FCSTD DOCUMENT  (FreeCAD 0.20R29603 (Git))
Label: Heat Exchanger inlet dispersion grid rounded edges
License: All rights reserved
LicenseURL: http://en.wikipedia.org/wiki/All_rights_reserved
objects: Sketcher::SketchObject×3, Spreadsheet::Sheet×1, PartDesign::Body×1
note: 4 computed .brp shape members not serialized (recipe doc carries the construction recipe); baked Part::Feature solids carry a one-line shape summary decoded from their .brp

FEATURE [Sketcher::SketchObject] Sketch
  Base_da = 2
  FullyConstrained = true
  MapMode = 5
  Support = -> [XY_Plane]
  expr: Constraints[100] = 5 * Base_da
  expr: Constraints[101] = 4 * Base_da
  expr: Constraints[102] = 3 * Base_da
  expr: Constraints[103] = 2 * Base_da
  expr: Constraints[105] = Base_da
  sketch-geometry (47):
    g0: LineSegment StartX=10 StartY=0 StartZ=0 EndX=10 EndY=10 EndZ=0
    g1: LineSegment StartX=20 StartY=0 StartZ=0 EndX=20.349 EndY=9.99391 EndZ=0
    g2: LineSegment StartX=10 StartY=0 StartZ=0 EndX=20 EndY=0 EndZ=0
    g3: LineSegment StartX=30 StartY=0 StartZ=0 EndX=31.0453 EndY=9.94522 EndZ=0
    g4: LineSegment StartX=20 StartY=0 StartZ=0 EndX=30 EndY=0 EndZ=0
    g5: LineSegment StartX=40 StartY=0 StartZ=0 EndX=42.0791 EndY=9.78148 EndZ=0
    g6: LineSegment StartX=30 StartY=0 StartZ=0 EndX=40 EndY=0 EndZ=0
    g7: LineSegment StartX=50 StartY=0 StartZ=0 EndX=53.4202 EndY=9.39693 EndZ=0
    g8: LineSegment StartX=40 StartY=0 StartZ=0 EndX=50 EndY=0 EndZ=0
    g9: LineSegment StartX=60 StartY=0 StartZ=0 EndX=65 EndY=8.66025 EndZ=0
    g10: LineSegment StartX=50 StartY=0 StartZ=0 EndX=60 EndY=0 EndZ=0
    g11: ArcOfCircle CenterX=0 CenterY=0 CenterZ=0 NormalX=0 NormalY=0 NormalZ=1 AngleXU=0 Radius=80 StartAngle=0 EndAngle=1.5708
    g12: ArcOfParabola CenterX=68.3381 CenterY=12.9026 CenterZ=0 NormalX=0 NormalY=0 NormalZ=1 Focal=8.86174 AngleXU=-0.816138 StartAngle=-5.33797 EndAngle=10.3906
    g13: GeomPoint X=74.4087 Y=6.44675 Z=0
    g14: LineSegment StartX=68.3381 StartY=12.9026 StartZ=0 EndX=74.4087 EndY=6.44675 EndZ=0
    g15: ArcOfParabola CenterX=75.2671 CenterY=35.9454 CenterZ=0 NormalX=0 NormalY=0 NormalZ=1 Focal=10.5647 AngleXU=-1.28196 StartAngle=-28.5038 EndAngle=-3.40911
    g16: GeomPoint X=78.2762 Y=25.8183 Z=0
    g17: LineSegment StartX=75.2671 StartY=35.9454 StartZ=0 EndX=78.2762 EndY=25.8183 EndZ=0
    g18: ArcOfParabola CenterX=69.0582 CenterY=53.9908 CenterZ=0 NormalX=0 NormalY=0 NormalZ=1 Focal=16.8881 AngleXU=-1.12039 StartAngle=-43.5341 EndAngle=-7.65215
    g19: GeomPoint X=76.4101 Y=38.7869 Z=0
    g20: LineSegment StartX=69.0582 StartY=53.9908 StartZ=0 EndX=76.4101 EndY=38.7869 EndZ=0
    g21: ArcOfParabola CenterX=58.9375 CenterY=71.8255 CenterZ=0 NormalX=0 NormalY=0 NormalZ=1 Focal=31.4249 AngleXU=-0.875633 StartAngle=-61.0548 EndAngle=-12.8996
    g22: GeomPoint X=79.0655 Y=47.6928 Z=0
    g23: LineSegment StartX=58.9375 StartY=71.8255 StartZ=0 EndX=79.0655 EndY=47.6928 EndZ=0
    g24: ArcOfParabola CenterX=41.678 CenterY=84.7017 CenterZ=0 NormalX=0 NormalY=0 NormalZ=1 Focal=64.3816 AngleXU=-0.560144 StartAngle=-74.6231 EndAngle=-14.3967
    g25: GeomPoint X=96.2207 Y=50.4952 Z=0
    g26: LineSegment StartX=41.678 StartY=84.7017 StartZ=0 EndX=96.2207 EndY=50.4952 EndZ=0
    g27: ArcOfParabola CenterX=10.3255 CenterY=-3.7979 CenterZ=0 NormalX=0 NormalY=0 NormalZ=1 Focal=146.058 AngleXU=0.0471993 StartAngle=13.7979 EndAngle=81.3483
    g28: GeomPoint X=156.22 Y=3.09336 Z=0
    g29: LineSegment StartX=10.3255 StartY=-3.7979 StartZ=0 EndX=156.22 EndY=3.09336 EndZ=0
    g30: LineSegment StartX=17.8017 StartY=77.9942 StartZ=0 EndX=3.6e-15 EndY=80 EndZ=0
    g31: LineSegment StartX=17.8017 StartY=77.9942 StartZ=0 EndX=34.7107 EndY=72.0775 EndZ=0
    g32: LineSegment StartX=34.7107 StartY=72.0775 StartZ=0 EndX=49.8792 EndY=62.5465 EndZ=0
    g33: LineSegment StartX=49.8792 StartY=62.5465 StartZ=0 EndX=62.5465 EndY=49.8792 EndZ=0
    g34: LineSegment StartX=62.5465 StartY=49.8792 StartZ=0 EndX=72.0775 EndY=34.7107 EndZ=0
    g35: LineSegment StartX=77.9942 StartY=17.8017 StartZ=0 EndX=72.0775 EndY=34.7107 EndZ=0
    g36: LineSegment StartX=77.9942 StartY=17.8017 StartZ=0 EndX=80 EndY=0 EndZ=0
    g37: LineSegment StartX=17.8017 StartY=77.9942 StartZ=0 EndX=20.0269 EndY=87.7435 EndZ=0
    g38: LineSegment StartX=77.9942 StartY=17.8017 StartZ=0 EndX=87.7435 EndY=20.0269 EndZ=0
    g39: LineSegment StartX=72.0775 StartY=34.7107 StartZ=0 EndX=81.0872 EndY=39.0495 EndZ=0
    g40: LineSegment StartX=62.5465 StartY=49.8792 StartZ=0 EndX=70.3648 EndY=56.1141 EndZ=0
    g41: LineSegment StartX=49.8792 StartY=62.5465 StartZ=0 EndX=56.1141 EndY=70.3648 EndZ=0
    g42: LineSegment StartX=34.7107 StartY=72.0775 StartZ=0 EndX=39.0495 EndY=81.0872 EndZ=0
    g43: LineSegment StartX=60 StartY=0 StartZ=0 EndX=70 EndY=0 EndZ=0
    g44: ArcOfCircle CenterX=75.2269 CenterY=0.670424 CenterZ=0 NormalX=0 NormalY=0 NormalZ=1 AngleXU=0 Radius=3.39097 StartAngle=0.467529 EndAngle=1.4226
    g45: ArcOfCircle CenterX=84.4513 CenterY=5.32744 CenterZ=0 NormalX=0 NormalY=0 NormalZ=1 AngleXU=0 Radius=6.94229 StartAngle=3.60912 EndAngle=4.01635
    g46: LineSegment StartX=70 StartY=0 StartZ=0 EndX=75.7276 EndY=4.02423 EndZ=0
  constraints (117):
    c: PointOnObject(g0,g-1)
    c: DistanceX(g-1,g0) = 10
    c: Coincident(g0,g2)
    c: Coincident(g1,g2)
    c: Distance(g2) = 10
    c: Coincident(g1,g4)
    c: Coincident(g3,g4)
    c: Equal(g2,g4)
    c: Parallel(g4,g2)
    c: Coincident(g3,g6)
    c: Coincident(g5,g6)
    c: Equal(g2,g6)
    c: Parallel(g6,g2)
    c: Coincident(g5,g8)
    c: Coincident(g7,g8)
    c: Equal(g2,g8)
    c: Parallel(g8,g2)
    c: Coincident(g7,g10)
    c: Coincident(g9,g10)
    c: Equal(g2,g10)
    c: Parallel(g10,g2)
    c: PointOnObject(g1,g-1)
    c: InternalAlignment(g13,g12)
    c: Coincident(g13,g14)
    c: Coincident(g12,g14)
    c: InternalAlignment(g16,g15)
    c: Coincident(g16,g17)
    c: Coincident(g15,g17)
    c: Tangent(g12,g9) = -1.5708
    c: Tangent(g15,g7) = -1.5708
    c: Equal(g9,g7)
    c: Equal(g7,g5)
    c: Equal(g5,g3)
    c: Equal(g3,g1)
    c: Equal(g1,g0)
    c: DistanceY(g0,g0) = 10
    c: PointOnObject(g15,g11)
    c: DistanceX(g11,g11) = 80
    c: Coincident(g-1,g11)
    c: PointOnObject(g11,g-1)
    c: PointOnObject(g12,g11)
    c: InternalAlignment(g19,g18)
    c: Coincident(g19,g20)
    c: Coincident(g18,g20)
    c: PointOnObject(g18,g11)
    c: InternalAlignment(g22,g21)
    c: Coincident(g22,g23)
    c: Coincident(g21,g23)
    c: PointOnObject(g21,g11)
    c: InternalAlignment(g25,g24)
    c: Coincident(g25,g26)
    c: Coincident(g24,g26)
    c: PointOnObject(g24,g11)
    c: InternalAlignment(g28,g27)
    c: Coincident(g28,g29)
    c: Coincident(g27,g29)
    c: PointOnObject(g27,g11)
    c: Tangent(g18,g5) = -1.5708
    c: Tangent(g21,g3) = -1.5708
    c: Tangent(g24,g1) = -1.5708
    c: Tangent(g27,g0) = -1.5708
    c: PointOnObject(g11,g-2)
    c: Coincident(g30,g27)
    c: Coincident(g30,g11)
    c: Coincident(g31,g27)
    c: Coincident(g31,g24)
    c: Coincident(g32,g24)
    c: Coincident(g32,g21)
    c: Coincident(g33,g21)
    c: Coincident(g33,g18)
    c: Coincident(g34,g18)
    c: Coincident(g34,g15)
    c: Coincident(g35,g12)
    c: Coincident(g35,g15)
    c: Coincident(g36,g12)
    c: Coincident(g36,g11)
    c: Equal(g36,g35)
    c: Equal(g35,g34)
    c: Equal(g33,g34)
    c: Equal(g32,g33)
    c: Equal(g31,g32)
    c: Equal(g30,g31)
    c: Perpendicular(g11,g38)
    c: Tangent(g38,g12) = -1.5708
    c: Perpendicular(g11,g39)
    c: Tangent(g39,g15) = -1.5708
    c: Perpendicular(g11,g40)
    c: Tangent(g40,g18) = -1.5708
    c: Perpendicular(g11,g41)
    c: Perpendicular(g11,g42)
    c: Tangent(g42,g24) = -1.5708
    c: Tangent(g41,g21) = -1.5708
    c: Equal(g38,g39)
    c: Equal(g39,g40)
    c: Equal(g40,g41)
    c: Equal(g41,g42)
    c: Equal(g42,g37)
    c: Distance(g37) = 10
    c: Tangent(g37,g27) = -1.5708
    c: Perpendicular(g11,g37)
    c: Angle(g9,g7) = 0.174533
    c: Angle(g7,g5) = 0.139626
    c: Angle(g5,g3) = 0.10472
    c: Angle(g3,g1) = 0.0698132
    c: Vertical(g0)
    c: Angle(g1,g0) = 0.0349066
    c: Coincident(g43,g9)
    c: Equal(g10,g43)
    c: Coincident(g45,g11)
    c: PointOnObject(g43,g-1)
    c: Coincident(g44,g46)
    c: Tangent(g44,g45) = 1.5708
    c: Coincident(g46,g43)
    c: Distance(g46) = 7
    c: Block(g46)
    c: Block(g44)
    c: Block(g45)
FEATURE [Sketcher::SketchObject] Sketch001
  ExternalGeometry = -> [Sketch]
  FullyConstrained = true
  MapMode = 5
  Support = -> [XY_Plane]
  expr: Constraints[24] = <<dim>>.A3
  sketch-geometry (47):
    g0: LineSegment StartX=10 StartY=10 StartZ=0 EndX=10 EndY=78.5848 EndZ=0
    g1: LineSegment StartX=20.349 StartY=9.99391 StartZ=0 EndX=22.589 EndY=74.1398 EndZ=0
    g2: LineSegment StartX=31.0453 StartY=9.94522 StartZ=0 EndX=36.9646 EndY=66.2635 EndZ=0
    g3: LineSegment StartX=42.0791 StartY=9.78148 StartZ=0 EndX=51.6203 EndY=54.6693 EndZ=0
    g4: LineSegment StartX=53.4202 StartY=9.39693 StartZ=0 EndX=64.438 EndY=39.6682 EndZ=0
    g5: LineSegment StartX=65 StartY=8.66025 StartZ=0 EndX=73.188 EndY=22.8423 EndZ=0
    g6: ArcOfCircle CenterX=9.1 CenterY=78.5848 CenterZ=0 NormalX=0 NormalY=0 NormalZ=1 AngleXU=0 Radius=0.9 StartAngle=1.2e-15 EndAngle=3.14159
    g7: ArcOfCircle CenterX=21.6896 CenterY=74.1712 CenterZ=0 NormalX=0 NormalY=0 NormalZ=1 AngleXU=0 Radius=0.9 StartAngle=6.24828 EndAngle=9.38987
    g8: ArcOfCircle CenterX=36.0695 CenterY=66.3576 CenterZ=0 NormalX=0 NormalY=0 NormalZ=1 AngleXU=0 Radius=0.9 StartAngle=6.17847 EndAngle=9.32006
    g9: ArcOfCircle CenterX=50.74 CenterY=54.8564 CenterZ=0 NormalX=0 NormalY=0 NormalZ=1 AngleXU=0 Radius=0.9 StartAngle=6.07375 EndAngle=9.21534
    g10: ArcOfCircle CenterX=63.5923 CenterY=39.976 CenterZ=0 NormalX=0 NormalY=0 NormalZ=1 AngleXU=0 Radius=0.9 StartAngle=5.93412 EndAngle=9.07571
    g11: ArcOfCircle CenterX=72.4086 CenterY=23.2923 CenterZ=0 NormalX=0 NormalY=0 NormalZ=1 AngleXU=0 Radius=0.9 StartAngle=5.75959 EndAngle=8.90118
    g12: LineSegment StartX=8.2 StartY=78.5848 StartZ=0 EndX=8.2 EndY=0 EndZ=0
    g13: LineSegment StartX=20.7901 StartY=74.2026 StartZ=0 EndX=18.2011 EndY=0.0628191 EndZ=0
    g14: LineSegment StartX=35.1744 StartY=66.4517 StartZ=0 EndX=28.2099 EndY=0.188151 EndZ=0
    g15: LineSegment StartX=49.8597 StartY=55.0436 StartZ=0 EndX=38.2393 EndY=0.374241 EndZ=0
    g16: LineSegment StartX=62.7466 StartY=40.2838 StartZ=0 EndX=48.3086 EndY=0.615636 EndZ=0
    g17: LineSegment StartX=71.6292 StartY=23.7423 StartZ=0 EndX=58.4412 EndY=0.9 EndZ=0
    g18: LineSegment StartX=8.2 StartY=0 StartZ=0 EndX=10 EndY=0 EndZ=0
    g19: LineSegment StartX=18.2011 StartY=0.0628191 StartZ=0 EndX=20 EndY=0 EndZ=0
    g20: LineSegment StartX=28.2099 StartY=0.188151 StartZ=0 EndX=30 EndY=0 EndZ=0
    g21: LineSegment StartX=38.2393 StartY=0.374241 StartZ=0 EndX=40 EndY=0 EndZ=0
    g22: LineSegment StartX=48.3086 StartY=0.615636 StartZ=0 EndX=50 EndY=0 EndZ=0
    g23: LineSegment StartX=58.4412 StartY=0.9 StartZ=0 EndX=60 EndY=1e-16 EndZ=0
    g24: LineSegment StartX=10 StartY=0 StartZ=0 EndX=10 EndY=-1.8 EndZ=0
    g25: LineSegment StartX=10 StartY=-1.8 StartZ=0 EndX=70 EndY=-1.8 EndZ=0
    g26: ArcOfCircle CenterX=41.1439 CenterY=3.22336 CenterZ=0 NormalX=0 NormalY=0 NormalZ=1 AngleXU=0 Radius=6.62447 StartAngle=5.93412 EndAngle=7.71233
    g27: ArcOfCircle CenterX=52.9459 CenterY=4.07267 CenterZ=0 NormalX=0 NormalY=0 NormalZ=1 AngleXU=0 Radius=5.34534 StartAngle=5.75959 EndAngle=7.76514
    g28: ArcOfCircle CenterX=29.5654 CenterY=2.21794 CenterZ=0 NormalX=0 NormalY=0 NormalZ=1 AngleXU=0 Radius=7.86771 StartAngle=6.07375 EndAngle=7.66476
    g29: ArcOfCircle CenterX=18.2589 CenterY=1.23404 CenterZ=0 NormalX=0 NormalY=0 NormalZ=1 AngleXU=0 Radius=9.00576 StartAngle=6.17847 EndAngle=7.61976
    g30: ArcOfCircle CenterX=7.26996 CenterY=0.444543 CenterZ=0 NormalX=0 NormalY=0 NormalZ=1 AngleXU=0 Radius=9.9378 StartAngle=6.24828 EndAngle=7.57569
    g31: LineSegment StartX=47.3689 StartY=0.957656 StartZ=0 EndX=48.3086 EndY=0.615636 EndZ=0
    g32: LineSegment StartX=37.2612 StartY=0.582153 StartZ=0 EndX=38.2393 EndY=0.374241 EndZ=0
    g33: LineSegment StartX=27.2153 StartY=0.29268 StartZ=0 EndX=28.2099 EndY=0.188151 EndZ=0
    g34: LineSegment StartX=17.2017 StartY=0.0977186 StartZ=0 EndX=18.2011 EndY=0.0628191 EndZ=0
    g35: LineSegment StartX=57.5751 StartY=1.4 StartZ=0 EndX=58.4412 EndY=0.9 EndZ=0
    g36: LineSegment StartX=57.5751 StartY=1.4 StartZ=0 EndX=52.9459 EndY=4.07267 EndZ=0
    g37: LineSegment StartX=47.3689 StartY=0.957656 StartZ=0 EndX=41.1439 EndY=3.22336 EndZ=0
    g38: LineSegment StartX=29.5654 StartY=2.21794 StartZ=0 EndX=37.2612 EndY=0.582153 EndZ=0
    g39: LineSegment StartX=18.2589 StartY=1.23404 StartZ=0 EndX=27.2153 EndY=0.29268 EndZ=0
    g40: LineSegment StartX=7.26996 StartY=0.444543 StartZ=0 EndX=17.2017 EndY=0.0977186 EndZ=0
    g41: LineSegment StartX=70 StartY=0 StartZ=0 EndX=70 EndY=-1.8 EndZ=0
    g42: LineSegment StartX=70 StartY=0 StartZ=0 EndX=71.0348 EndY=-1.47282 EndZ=0
    g43: LineSegment StartX=71.0348 StartY=-1.47282 StartZ=0 EndX=81.7256 EndY=6.03854 EndZ=0
    g44: LineSegment StartX=81.7256 StartY=6.03854 StartZ=0 EndX=80.6908 EndY=7.51136 EndZ=0
    g45: LineSegment StartX=80.6908 StartY=7.51136 StartZ=0 EndX=75.7276 EndY=4.02423 EndZ=0
    g46: ArcOfCircle CenterX=66.5865 CenterY=-2.39833 CenterZ=0 NormalX=0 NormalY=0 NormalZ=1 AngleXU=0 Radius=11.1718 StartAngle=0.61247 EndAngle=1.71329
  constraints (118):
    c: Distance(g5) = 16.376
    c: Distance(g4) = 32.214
    c: Distance(g3) = 45.8907
    c: Distance(g2) = 56.6285
    c: Distance(g1) = 64.185
    c: Distance(g0) = 68.5848
    c: Vertical(g12)
    c: Coincident(g18,g12)
    c: Coincident(g19,g13)
    c: Coincident(g20,g14)
    c: Coincident(g21,g15)
    c: Coincident(g22,g16)
    c: Coincident(g23,g17)
    c: Perpendicular(g18,g12)
    c: Perpendicular(g13,g19)
    c: Perpendicular(g14,g20)
    c: Perpendicular(g15,g21)
    c: Perpendicular(g16,g22)
    c: Perpendicular(g17,g23)
    c: Equal(g18,g19)
    c: Equal(g19,g20)
    c: Equal(g20,g21)
    c: Equal(g21,g22)
    c: Equal(g22,g23)
    c: Distance(g18) = 1.8
    c: Parallel(g13,g1)
    c: Parallel(g14,g2)
    c: Parallel(g15,g3)
    c: Parallel(g16,g4)
    c: Parallel(g17,g5)
    c: Tangent(g12,g6) = -1.5708
    c: Tangent(g6,g0) = -1.5708
    c: Tangent(g13,g7) = -1.5708
    c: Tangent(g7,g1) = -1.5708
    c: Tangent(g14,g8) = -1.5708
    c: Tangent(g8,g2) = -1.5708
    c: Tangent(g15,g9) = -1.5708
    c: Tangent(g9,g3) = -1.5708
    c: Tangent(g16,g10) = -1.5708
    c: Tangent(g10,g4) = -1.5708
    c: Tangent(g17,g11) = -1.5708
    c: Tangent(g11,g5) = -1.5708
    c: Coincident(g18,g24)
    c: Vertical(g24)
    c: Coincident(g24,g25)
    c: Horizontal(g25)
    c: Coincident(g27,g4)
    c: Coincident(g31,g26)
    c: Coincident(g31,g16)
    c: Coincident(g32,g28)
    c: Coincident(g32,g15)
    c: Coincident(g33,g29)
    c: Coincident(g33,g14)
    c: Coincident(g34,g30)
    c: Coincident(g34,g13)
    c: Parallel(g34,g19)
    c: Parallel(g33,g20)
    c: Parallel(g32,g21)
    c: Parallel(g31,g22)
    c: Coincident(g35,g27)
    c: Coincident(g35,g17)
    c: Parallel(g35,g23)
    c: Equal(g35,g31)
    c: Equal(g31,g32)
    c: Equal(g32,g33)
    c: Equal(g33,g34)
    c: Distance(g35) = 1
    c: Coincident(g36,g27)
    c: Coincident(g26,g37)
    c: Coincident(g38,g28)
    c: Coincident(g38,g28)
    c: Coincident(g39,g29)
    c: Coincident(g39,g29)
    c: Coincident(g40,g30)
    c: Coincident(g40,g30)
    c: Parallel(g40,g34)
    c: Parallel(g39,g33)
    c: Parallel(g38,g32)
    c: Parallel(g37,g31)
    c: Coincident(g26,g37)
    c: Parallel(g36,g35)
    c: Coincident(g36,g27)
    c: Coincident(g41,g25)
    c: Vertical(g41)
    c: Equal(g18,g24)
    c: Coincident(g41,g-9)
    c: Coincident(g23,g-8)
    c: Coincident(g5,g-8)
    c: Parallel(g-8,g5)
    c: Coincident(g22,g-7)
    c: Parallel(g4,g-7)
    c: Coincident(g4,g-7)
    c: Coincident(g21,g-6)
    c: Tangent(g3,g-6) = -1.5708
    c: Coincident(g26,g3)
    c: Coincident(g19,g-4)
    c: Coincident(g20,g-5)
    c: Tangent(g1,g-4) = -1.5708
    c: Tangent(g0,g-3) = -1.5708
    c: Tangent(g2,g-5) = -1.5708
    c: Coincident(g18,g-3)
    c: Coincident(g29,g1)
    c: Coincident(g30,g0)
    c: Coincident(g2,g28)
    c: Coincident(g41,g42)
    c: Coincident(g42,g43)
    c: Coincident(g43,g44)
    c: Coincident(g44,g45)
    c: Perpendicular(g44,g45)
    c: Perpendicular(g43,g42)
    c: Parallel(g-9,g45)
    c: Parallel(g45,g43)
    c: Equal(g23,g42)
    c: Distance(g45) = 6.06573
    c: Coincident(g46,g5)
    c: Coincident(g46,g45)
    c: Coincident(g-9,g45)
    c: Perpendicular(g46,g45)
FEATURE [Spreadsheet::Sheet] Spreadsheet  label="dim"
  cells = A2=channel width; A3=1.8
FEATURE [Sketcher::SketchObject] Sketch003
  ExternalGeometry = -> [Sketch001,Sketch]
  FullyConstrained = false
  MapMode = 5
  Support = -> [XY_Plane]
  expr: Constraints[100] = Sketch.Constraints[102]
  expr: Constraints[101] = Sketch.Constraints[103]
  expr: Constraints[103] = Sketch.Constraints[105]
  expr: Constraints[1] = Sketch.Constraints[1]
  expr: Constraints[35] = Sketch.Constraints[35]
  expr: Constraints[4] = Sketch.Constraints[4]
  expr: Constraints[95] = Sketch.Constraints[97]
  expr: Constraints[98] = Sketch.Constraints[100]
  expr: Constraints[99] = Sketch.Constraints[101]
  sketch-geometry (80):
    g0: LineSegment StartX=10 StartY=0 StartZ=0 EndX=10 EndY=10 EndZ=0
    g1: LineSegment StartX=20 StartY=0 StartZ=0 EndX=20.349 EndY=9.99391 EndZ=0
    g2: LineSegment StartX=10 StartY=0 StartZ=0 EndX=20 EndY=0 EndZ=0
    g3: LineSegment StartX=30 StartY=0 StartZ=0 EndX=31.0453 EndY=9.94522 EndZ=0
    g4: LineSegment StartX=20 StartY=0 StartZ=0 EndX=30 EndY=0 EndZ=0
    g5: LineSegment StartX=40 StartY=0 StartZ=0 EndX=42.0791 EndY=9.78148 EndZ=0
    g6: LineSegment StartX=30 StartY=0 StartZ=0 EndX=40 EndY=0 EndZ=0
    g7: LineSegment StartX=50 StartY=0 StartZ=0 EndX=53.4202 EndY=9.39693 EndZ=0
    g8: LineSegment StartX=40 StartY=0 StartZ=0 EndX=50 EndY=0 EndZ=0
    g9: LineSegment StartX=60 StartY=0 StartZ=0 EndX=65 EndY=8.66025 EndZ=0
    g10: LineSegment StartX=50 StartY=0 StartZ=0 EndX=60 EndY=0 EndZ=0
    g11: ArcOfCircle CenterX=0 CenterY=0 CenterZ=0 NormalX=0 NormalY=0 NormalZ=1 AngleXU=0 Radius=80 StartAngle=-8.01048e-11 EndAngle=1.5708
    g12: ArcOfParabola CenterX=68.3381 CenterY=12.9026 CenterZ=0 NormalX=0 NormalY=0 NormalZ=1 Focal=8.86174 AngleXU=-0.816138 StartAngle=-5.33797 EndAngle=10.3906
    g13: GeomPoint X=74.4087 Y=6.44675 Z=0
    g14: LineSegment StartX=68.3381 StartY=12.9026 StartZ=0 EndX=74.4087 EndY=6.44675 EndZ=0
    g15: ArcOfParabola CenterX=75.2671 CenterY=35.9454 CenterZ=0 NormalX=0 NormalY=0 NormalZ=1 Focal=10.5647 AngleXU=-1.28196 StartAngle=-28.5038 EndAngle=-3.40911
    g16: GeomPoint X=78.2762 Y=25.8183 Z=0
    g17: LineSegment StartX=75.2671 StartY=35.9454 StartZ=0 EndX=78.2762 EndY=25.8183 EndZ=0
    g18: ArcOfParabola CenterX=69.0582 CenterY=53.9908 CenterZ=0 NormalX=0 NormalY=0 NormalZ=1 Focal=16.8881 AngleXU=-1.12039 StartAngle=-43.5341 EndAngle=-7.65215
    g19: GeomPoint X=76.4101 Y=38.7869 Z=0
    g20: LineSegment StartX=69.0582 StartY=53.9908 StartZ=0 EndX=76.4101 EndY=38.7869 EndZ=0
    g21: ArcOfParabola CenterX=58.9375 CenterY=71.8255 CenterZ=0 NormalX=0 NormalY=0 NormalZ=1 Focal=31.4249 AngleXU=-0.875633 StartAngle=-61.0548 EndAngle=-12.8996
    g22: GeomPoint X=79.0655 Y=47.6928 Z=0
    g23: LineSegment StartX=58.9375 StartY=71.8255 StartZ=0 EndX=79.0655 EndY=47.6928 EndZ=0
    g24: ArcOfParabola CenterX=41.678 CenterY=84.7017 CenterZ=0 NormalX=0 NormalY=0 NormalZ=1 Focal=64.3816 AngleXU=-0.560144 StartAngle=-74.6231 EndAngle=-14.3967
    g25: GeomPoint X=96.2207 Y=50.4952 Z=0
    g26: LineSegment StartX=41.678 StartY=84.7017 StartZ=0 EndX=96.2207 EndY=50.4952 EndZ=0
    g27: ArcOfParabola CenterX=10.3255 CenterY=-3.79791 CenterZ=0 NormalX=0 NormalY=0 NormalZ=1 Focal=146.058 AngleXU=0.0471993 StartAngle=13.7979 EndAngle=81.3483
    g28: GeomPoint X=156.22 Y=3.09336 Z=0
    g29: LineSegment StartX=10.3255 StartY=-3.79791 StartZ=0 EndX=156.22 EndY=3.09336 EndZ=0
    g30: LineSegment StartX=17.8017 StartY=77.9942 StartZ=0 EndX=3.6e-15 EndY=80 EndZ=0
    g31: LineSegment StartX=17.8017 StartY=77.9942 StartZ=0 EndX=34.7107 EndY=72.0775 EndZ=0
    g32: LineSegment StartX=34.7107 StartY=72.0775 StartZ=0 EndX=49.8792 EndY=62.5465 EndZ=0
    g33: LineSegment StartX=49.8792 StartY=62.5465 StartZ=0 EndX=62.5465 EndY=49.8792 EndZ=0
    g34: LineSegment StartX=62.5465 StartY=49.8792 StartZ=0 EndX=72.0775 EndY=34.7107 EndZ=0
    g35: LineSegment StartX=77.9942 StartY=17.8017 StartZ=0 EndX=72.0775 EndY=34.7107 EndZ=0
    g36: LineSegment StartX=77.9942 StartY=17.8017 StartZ=0 EndX=80 EndY=-6.4084e-09 EndZ=0
    g37: LineSegment StartX=17.8017 StartY=77.9942 StartZ=0 EndX=20.0269 EndY=87.7435 EndZ=0
    g38: LineSegment StartX=77.9942 StartY=17.8017 StartZ=0 EndX=87.7435 EndY=20.0269 EndZ=0
    g39: LineSegment StartX=72.0775 StartY=34.7107 StartZ=0 EndX=81.0872 EndY=39.0495 EndZ=0
    g40: LineSegment StartX=62.5465 StartY=49.8792 StartZ=0 EndX=70.3648 EndY=56.1141 EndZ=0
    g41: LineSegment StartX=49.8792 StartY=62.5465 StartZ=0 EndX=56.1141 EndY=70.3648 EndZ=0
    g42: LineSegment StartX=34.7107 StartY=72.0775 StartZ=0 EndX=39.0495 EndY=81.0872 EndZ=0
    g43: LineSegment StartX=60 StartY=0 StartZ=0 EndX=70 EndY=0 EndZ=0
    g44: ArcOfCircle CenterX=84.4513 CenterY=5.32744 CenterZ=0 NormalX=0 NormalY=0 NormalZ=1 AngleXU=0 Radius=6.94229 StartAngle=3.60912 EndAngle=4.01635
    g45: LineSegment StartX=70 StartY=0 StartZ=0 EndX=75.7276 EndY=4.02423 EndZ=0
    g46: ArcOfCircle CenterX=21.8708 CenterY=73.5796 CenterZ=0 NormalX=0 NormalY=0 NormalZ=1 AngleXU=0 Radius=2.10178 StartAngle=2.01896 EndAngle=3.10669
    g47: ArcOfCircle CenterX=37.6679 CenterY=65.3413 CenterZ=0 NormalX=0 NormalY=0 NormalZ=1 AngleXU=0 Radius=3.59582 StartAngle=1.73188 EndAngle=3.03687
    g48: ArcOfCircle CenterX=54.572 CenterY=53.5281 CenterZ=0 NormalX=0 NormalY=0 NormalZ=1 AngleXU=0 Radius=5.92442 StartAngle=1.93894 EndAngle=2.93215
    g49: ArcOfCircle CenterX=71.4268 CenterY=38.9124 CenterZ=0 NormalX=0 NormalY=0 NormalZ=1 AngleXU=0 Radius=9.62576 StartAngle=2.25286 EndAngle=2.79253
    g50: LineSegment StartX=19.7703 StartY=73.653 StartZ=0 EndX=17.1668 EndY=-0.901672 EndZ=0
    g51: LineSegment StartX=34.0917 StartY=65.7172 StartZ=0 EndX=27.1108 EndY=-0.701842 EndZ=0
    g52: LineSegment StartX=48.777 StartY=54.7599 StartZ=0 EndX=37.0533 EndY=-0.395995 EndZ=0
    g53: LineSegment StartX=62.3815 StartY=42.2046 StartZ=0 EndX=47.0268 EndY=0.0179638 EndZ=0
    g54: LineSegment StartX=74.993 StartY=31.5686 StartZ=0 EndX=57.0751 EndY=0.533975 EndZ=0
    g55: ArcOfCircle CenterX=73.0506 CenterY=32.69 CenterZ=0 NormalX=0 NormalY=0 NormalZ=1 AngleXU=0 Radius=2.24282 StartAngle=5.75959 EndAngle=8.30278
    g56: ArcOfCircle CenterX=63.9449 CenterY=48.1257 CenterZ=0 NormalX=0 NormalY=0 NormalZ=1 AngleXU=0 Radius=2.24282 StartAngle=5.39445 EndAngle=8.52718
    g57: ArcOfCircle CenterX=51.6327 CenterY=61.1481 CenterZ=0 NormalX=0 NormalY=0 NormalZ=1 AngleXU=0 Radius=2.24282 StartAngle=5.08054 EndAngle=8.75158
    g58: ArcOfCircle CenterX=36.7314 CenterY=71.1044 CenterZ=0 NormalX=0 NormalY=0 NormalZ=1 AngleXU=0 Radius=2.24282 StartAngle=4.87347 EndAngle=8.97598
    g59: ArcOfCircle CenterX=19.9883 CenterY=77.4952 CenterZ=0 NormalX=0 NormalY=0 NormalZ=1 AngleXU=0 Radius=2.24282 StartAngle=5.16055 EndAngle=9.20038
    g60: GeomPoint X=77.5717 Y=3.12003 Z=0
    g61: ArcOfCircle CenterX=78.4933 CenterY=15.6151 CenterZ=0 NormalX=0 NormalY=0 NormalZ=1 AngleXU=0 Radius=2.24282 StartAngle=4.98456 EndAngle=8.07838
    g62: ArcOfCircle CenterX=80.7445 CenterY=7.54912 CenterZ=0 NormalX=0 NormalY=0 NormalZ=1 AngleXU=0 Radius=6.13142 StartAngle=1.84297 EndAngle=3.75406
    g63: LineSegment StartX=60 StartY=0 StartZ=0 EndX=59.5 EndY=-0.866025 EndZ=0
    g64: LineSegment StartX=50 StartY=0 StartZ=0 EndX=49.658 EndY=-0.939693 EndZ=0
    g65: LineSegment StartX=40 StartY=0 StartZ=0 EndX=39.7921 EndY=-0.978148 EndZ=0
    g66: LineSegment StartX=30 StartY=0 StartZ=0 EndX=29.8955 EndY=-0.994522 EndZ=0
    g67: LineSegment StartX=20 StartY=0 StartZ=0 EndX=19.9651 EndY=-0.999391 EndZ=0
    g68: GeomPoint X=20.349 Y=9.99391 Z=0
    g69: LineSegment StartX=10 StartY=0 StartZ=0 EndX=10 EndY=-16.0092 EndZ=0
    g70: LineSegment StartX=80 StartY=-6.4084e-09 StartZ=0 EndX=80 EndY=-16.0092 EndZ=0
    g71: LineSegment StartX=57.0751 StartY=0.533975 StartZ=0 EndX=59.5 EndY=-0.866025 EndZ=0
    g72: LineSegment StartX=49.658 StartY=-0.939693 StartZ=0 EndX=47.0268 EndY=0.0179638 EndZ=0
    g73: LineSegment StartX=39.7921 StartY=-0.978148 StartZ=0 EndX=37.0533 EndY=-0.395995 EndZ=0
    g74: LineSegment StartX=29.8955 StartY=-0.994522 StartZ=0 EndX=27.1108 EndY=-0.701842 EndZ=0
    g75: LineSegment StartX=19.9651 StartY=-0.999391 StartZ=0 EndX=17.1668 EndY=-0.901672 EndZ=0
    g76: LineSegment StartX=80 StartY=-16.0092 StartZ=0 EndX=10 EndY=-16.0092 EndZ=0
    g77: LineSegment StartX=70 StartY=0 StartZ=0 EndX=69.1818 EndY=-0.57489 EndZ=0
    g78: LineSegment StartX=69.1818 StartY=-0.57489 StartZ=0 EndX=70.8755 EndY=-2.98549 EndZ=0
    g79: LineSegment StartX=70.8755 StartY=-2.98549 StartZ=0 EndX=78.254 EndY=2.19867 EndZ=0
  constraints (189):
    c: PointOnObject(g0,g-1)
    c: DistanceX(g-1,g0) = 10
    c: Coincident(g0,g2)
    c: Coincident(g1,g2)
    c: Distance(g2) = 10
    c: Coincident(g1,g4)
    c: Coincident(g3,g4)
    c: Equal(g2,g4)
    c: Parallel(g4,g2)
    c: Coincident(g3,g6)
    c: Coincident(g5,g6)
    c: Equal(g2,g6)
    c: Parallel(g6,g2)
    c: Coincident(g5,g8)
    c: Coincident(g7,g8)
    c: Equal(g2,g8)
    c: Parallel(g8,g2)
    c: Coincident(g7,g10)
    c: Coincident(g9,g10)
    c: Equal(g2,g10)
    c: Parallel(g10,g2)
    c: PointOnObject(g1,g-1)
    c: InternalAlignment(g13,g12)
    c: Coincident(g13,g14)
    c: Coincident(g12,g14)
    c: InternalAlignment(g16,g15)
    c: Coincident(g16,g17)
    c: Coincident(g15,g17)
    c: Tangent(g12,g9) = -1.5708
    c: Tangent(g15,g7) = -1.5708
    c: Equal(g9,g7)
    c: Equal(g7,g5)
    c: Equal(g5,g3)
    c: Equal(g3,g1)
    c: Equal(g1,g0)
    c: DistanceY(g0,g0) = 10
    c: PointOnObject(g15,g11)
    c: Coincident(g-1,g11)
    c: PointOnObject(g12,g11)
    c: InternalAlignment(g19,g18)
    c: Coincident(g19,g20)
    c: Coincident(g18,g20)
    c: PointOnObject(g18,g11)
    c: InternalAlignment(g22,g21)
    c: Coincident(g22,g23)
    c: Coincident(g21,g23)
    c: PointOnObject(g21,g11)
    c: InternalAlignment(g25,g24)
    c: Coincident(g25,g26)
    c: Coincident(g24,g26)
    c: PointOnObject(g24,g11)
    c: InternalAlignment(g28,g27)
    c: Coincident(g28,g29)
    c: Coincident(g27,g29)
    c: PointOnObject(g27,g11)
    c: Tangent(g18,g5) = -1.5708
    c: Tangent(g21,g3) = -1.5708
    c: Tangent(g24,g1) = -1.5708
    c: Tangent(g27,g0) = -1.5708
    c: PointOnObject(g11,g-2)
    c: Coincident(g30,g27)
    c: Coincident(g30,g11)
    c: Coincident(g31,g27)
    c: Coincident(g31,g24)
    c: Coincident(g32,g24)
    c: Coincident(g32,g21)
    c: Coincident(g33,g21)
    c: Coincident(g33,g18)
    c: Coincident(g34,g18)
    c: Coincident(g34,g15)
    c: Coincident(g35,g12)
    c: Coincident(g35,g15)
    c: Coincident(g36,g12)
    c: Coincident(g36,g11)
    c: Equal(g36,g35)
    c: Equal(g35,g34)
    c: Equal(g33,g34)
    c: Equal(g32,g33)
    c: Equal(g31,g32)
    c: Equal(g30,g31)
    c: Perpendicular(g11,g38)
    c: Tangent(g38,g12) = -1.5708
    c: Perpendicular(g11,g39)
    c: Tangent(g39,g15) = -1.5708
    c: Perpendicular(g11,g40)
    c: Tangent(g40,g18) = -1.5708
    c: Perpendicular(g11,g41)
    c: Perpendicular(g11,g42)
    c: Tangent(g42,g24) = -1.5708
    c: Tangent(g41,g21) = -1.5708
    c: Equal(g38,g39)
    c: Equal(g39,g40)
    c: Equal(g40,g41)
    c: Equal(g41,g42)
    c: Equal(g42,g37)
    c: Distance(g37) = 10
    c: Tangent(g37,g27) = -1.5708
    c: Perpendicular(g11,g37)
    c: Angle(g9,g7) = 0.174533
    c: Angle(g7,g5) = 0.139626
    c: Angle(g5,g3) = 0.10472
    c: Angle(g3,g1) = 0.0698132
    c: Vertical(g0)
    c: Angle(g1,g0) = 0.0349066
    c: Coincident(g43,g9)
    c: Equal(g10,g43)
    c: Coincident(g44,g11)
    c: PointOnObject(g43,g-1)
    c: Coincident(g45,g43)
    c: Block(g45)
    c: Block(g44)
    c: Tangent(g50,g46) = -1.5708
    c: Tangent(g51,g47) = -1.5708
    c: Tangent(g52,g48) = -1.5708
    c: Tangent(g53,g49) = -1.5708
    c: Parallel(g54,g-12)
    c: Parallel(g53,g-11)
    c: Parallel(g-10,g52)
    c: Parallel(g-9,g51)
    c: Parallel(g-8,g50)
    c: Tangent(g59,g46) = 1.5708
    c: Tangent(g59,g27) = 1.5708
    c: Tangent(g58,g47) = 1.5708
    c: Tangent(g58,g24) = 1.5708
    c: PointOnObject(g-4,g50)
    c: PointOnObject(g-3,g51)
    c: PointOnObject(g-5,g52)
    c: PointOnObject(g-6,g53)
    c: PointOnObject(g-7,g54)
    c: Tangent(g57,g48) = 1.5708
    c: Tangent(g57,g21) = 1.5708
    c: Tangent(g56,g49) = 1.5708
    c: Tangent(g56,g18) = 1.5708
    c: Tangent(g55,g15) = 1.5708
    c: Equal(g59,g58)
    c: Equal(g58,g57)
    c: Equal(g57,g56)
    c: Equal(g56,g55)
    c: Tangent(g54,g55) = 1.5708
    c: PointOnObject(g60,g-13)
    c: Coincident(g62,g45)
    c: Perpendicular(g62,g45)
    c: Tangent(g62,g61) = 1.5708
    c: Equal(g55,g61)
    c: Tangent(g61,g12) = 1.5708
    c: Coincident(g67,g1)
    c: Tangent(g66,g3) = 1.5708
    c: Tangent(g65,g5) = 1.5708
    c: Tangent(g64,g7) = 1.5708
    c: Tangent(g63,g9) = 1.5708
    c: PointOnObject(g68,g24)
    c: PointOnObject(g68,g67)
    c: Tangent(g24,g67,g68) = 1.5708
    c: Coincident(g69,g0)
    c: Vertical(g69)
    c: Coincident(g70,g44)
    c: Vertical(g70)
    c: Coincident(g71,g54)
    c: Coincident(g71,g63)
    c: Coincident(g72,g64)
    c: Coincident(g72,g53)
    c: Coincident(g73,g65)
    c: Coincident(g73,g52)
    c: Coincident(g74,g66)
    c: Coincident(g74,g51)
    c: Coincident(g75,g67)
    c: Coincident(g75,g50)
    c: Perpendicular(g75,g50)
    c: Perpendicular(g74,g51)
    c: Perpendicular(g73,g52)
    c: Perpendicular(g72,g53)
    c: Perpendicular(g71,g54)
    c: Coincident(g76,g70)
    c: Coincident(g76,g69)
    c: Horizontal(g76)
    c: Equal(g67,g66)
    c: Equal(g66,g65)
    c: Equal(g65,g64)
    c: Equal(g64,g63)
    c: Coincident(g77,g78)
    c: Coincident(g78,g79)
    c: Perpendicular(g77,g78)
    c: Parallel(g77,g79)
    c: Equal(g63,g77)
    c: Coincident(g77,g45)
    c: PointOnObject(g44,g79)
    c: PointOnObject(g79,g-14)
    c: Distance(g64) = 1
    c: Parallel(g77,g45)
FEATURE [PartDesign::Body] Body
  Group = -> [Sketch,Sketch001,Sketch003]
  Origin = -> Origin
